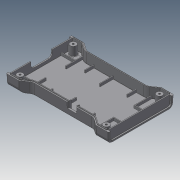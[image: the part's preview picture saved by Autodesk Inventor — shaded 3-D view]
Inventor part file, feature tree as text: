
AUTODESK INVENTOR PART (.ipt)
format: ipt  version: 2020.3 (Build 243373000, 373)  size: 737,792 bytes
history: native  units: in
note: dims shown in document units (in); Inventor stores cm internally (conversion verified against a paired STEP export)
features: fillet x1
ambient origin geometry x8: Origin, YZ Plane, XZ Plane, XY Plane, X Axis, Y Axis, Z Axis, Center Point
bodies: Solid1 (feature_tree)
feature tree (1):
  fillet  "Fillet14"  [1 undecoded]
note: 1 required parameter value undecoded (feature->parameter linkage not recoverable at this tier; creation-order binding heuristic only, values carry confidence <= 0.55)
